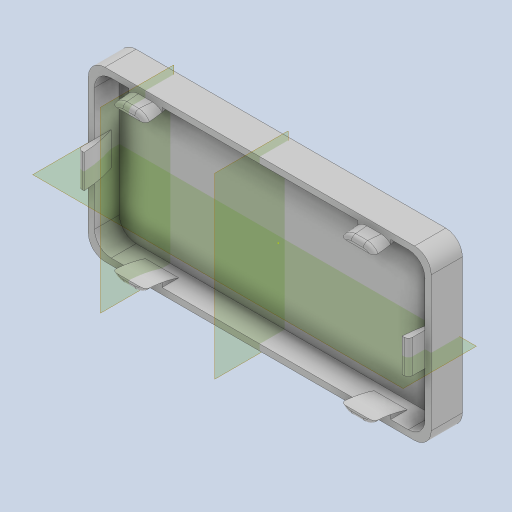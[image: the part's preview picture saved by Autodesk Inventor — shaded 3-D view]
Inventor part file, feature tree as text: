
AUTODESK INVENTOR PART (.ipt)
format: ipt  version: 2024 (Build 280153000, 153)  size: 814,592 bytes
history: native  units: mm
features: fillet x9, sketch x8, extrude x7, other x6, mirror x6, plane x3
ambient origin geometry x8: Origin, YZ Plane, XZ Plane, XY Plane, X Axis, Y Axis, Z Axis, Center Point
bodies: Body1 (feature_tree)
feature tree (39):
  other  "Sólido1"
  extrude  "Extrusión1"  Depth=1.5mm
  extrude  "Extrusión2"  Depth=14.0mm
  extrude  "Extrusión3"  Depth=20.75mm
  fillet  "Empalme1"  Radius=13.75mm
  plane  "Plano de trabajo1"
  plane  "Plano de trabajo2"
  extrude  "Extrusión4"  Depth=2.0mm
  fillet  "Empalme2"  Radius=16.0mm
  mirror  "Simetría1"
  mirror  "Simetría2"
  fillet  "Empalme3"  Radius=2.0mm
  sketch  "Boceto5"  dims[d17=39.75mm d18=18.75mm d24=8.0mm d25=30.0mm]
  extrude  "Extrusión5"  Depth=18.75mm
  fillet  "Empalme4"  Radius=8.0mm
  fillet  "Empalme5"  Radius=30.0mm
  mirror  "Simetría3"
  extrude  "Extrusión6"  Depth=8.0mm TaperAngle=0.0deg
  fillet  "Empalme6"  Radius=2.0mm
  fillet  "Empalme7"  Radius=4.0mm
  mirror  "Simetría4"
  plane  "Plano de trabajo3"
  extrude  "Extrusión7"  Depth=8.0mm
  fillet  "Empalme8"  Radius=30.0mm
  fillet  "Empalme9"  Radius=8.0mm
  mirror  "Simetría5"
  mirror  "Simetría6"
  sketch  "Boceto1"  dims[d4=0.0mm d5=1.5mm]
  sketch  "Boceto2"  dims[d6=6.0mm d7=0.0mm d8=14.0mm]
  sketch  "Boceto3"  dims[d9=9.0mm d10=20.75mm d11=13.75mm]
  sketch  "Boceto4"  dims[d12=12.75mm d13=2.0mm d14=16.0mm d15=0.0mm d16=2.0mm]
  sketch  "Boceto6"  dims[d26=1.5mm d27=8.0mm d28=0.0mm d29=2.0mm d30=4.0mm]
  sketch  "Boceto7"  dims[d31=1.5mm d32=8.0mm d33=30.0mm d34=8.0mm d35=0.0mm]
  sketch  "Boceto8"  dims[d36=3.0mm d37=1.0mm d38=1.5mm d39=8.0mm d40=30.0mm d41=8.0mm d42=0.0mm d43=3.0mm d44=1.0mm d45=27.5mm d46=1.5mm d47=8.0mm d48=30.0mm d49=1.5mm d50=8.0mm d51=0.0mm d52=3.0mm d53=1.0mm]
  other  "Proyectar aristas de corte1"
  other  "Proyectar aristas de corte2"
  other  "Proyectar aristas de corte3"
  other  "Proyectar aristas de corte4"
  other  "Proyectar aristas de corte5"
